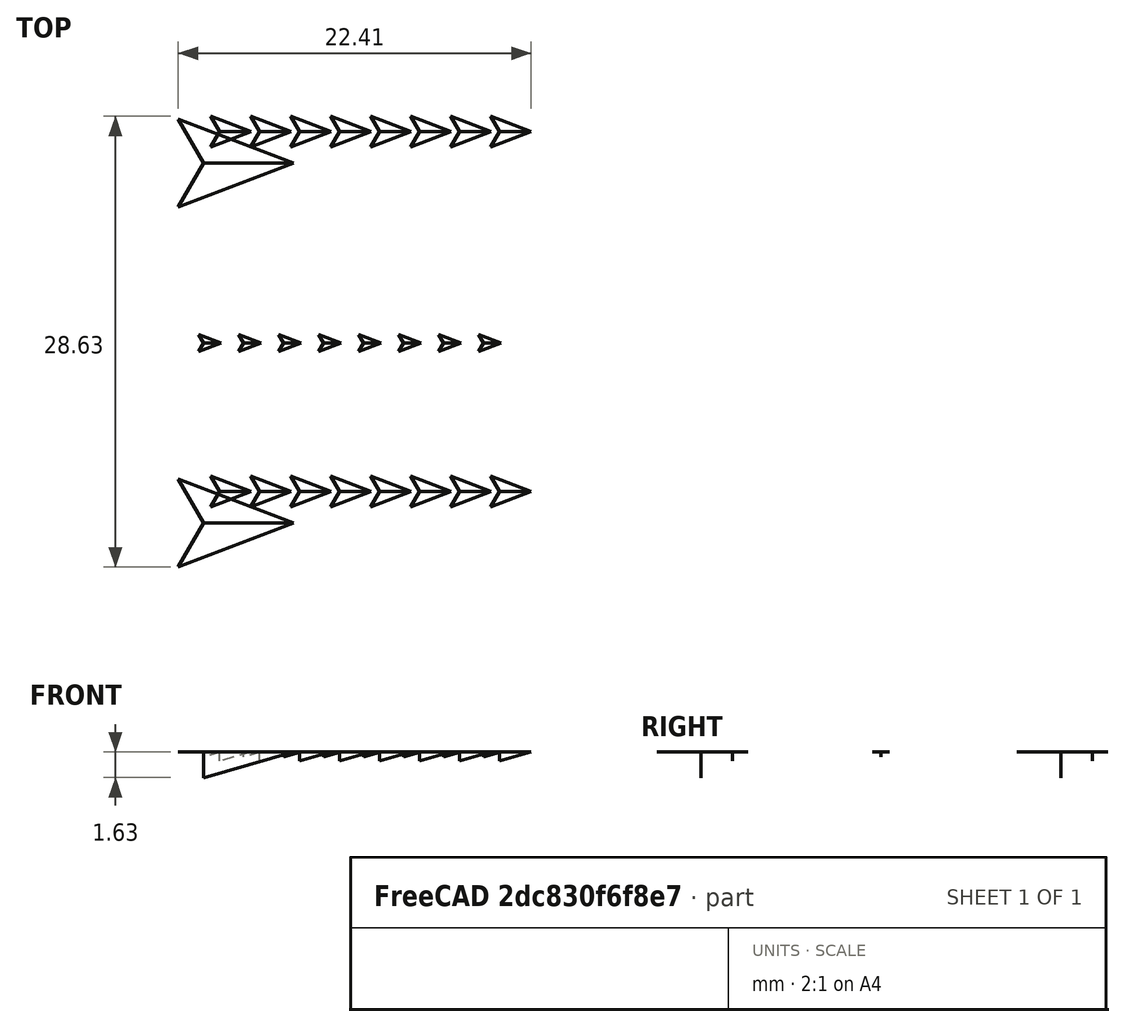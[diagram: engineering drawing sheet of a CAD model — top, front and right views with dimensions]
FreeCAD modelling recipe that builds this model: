
FCSTD DOCUMENT  (FreeCAD 0.22R34729 (Git))
Label: el_scheme_cut
License: All rights reserved
LicenseURL: http://en.wikipedia.org/wiki/All_rights_reserved
objects: Sketcher::SketchObject×3, Part::FeaturePython×3, Image::ImagePlane×1
note: 6 computed .brp shape members not serialized (recipe doc carries the construction recipe); baked Part::Feature solids carry a one-line shape summary decoded from their .brp

FEATURE [Sketcher::SketchObject] Sketch
  FullyConstrained = false
  sketch-geometry (1):
    g0: LineSegment StartX=6.30828 StartY=-11.43 StartZ=0 EndX=6.30828 EndY=11.43 EndZ=0
  constraints (2):
    c: Symmetric(g0,g0,g-1)
    c: DistanceY(g0,g0) = 22.86
FEATURE [Sketcher::SketchObject] Sketch001
  FullyConstrained = true
  sketch-geometry (5):
    g0: LineSegment StartX=34.2 StartY=-12.8 StartZ=0 EndX=34.2 EndY=12.8 EndZ=0
    g1: LineSegment StartX=34.2 StartY=12.8 StartZ=0 EndX=0 EndY=12.8 EndZ=0
    g2: LineSegment StartX=0 StartY=12.8 StartZ=0 EndX=0 EndY=-12.8 EndZ=0
    g3: LineSegment StartX=0 StartY=-12.8 StartZ=0 EndX=34.2 EndY=-12.8 EndZ=0
    g4: GeomPoint X=17.1 Y=0 Z=0
  constraints (13):
    c: Coincident(g0,g1)
    c: Coincident(g1,g2)
    c: Coincident(g2,g3)
    c: Coincident(g3,g0)
    c: Horizontal(g1)
    c: Horizontal(g3)
    c: Vertical(g0)
    c: Vertical(g2)
    c: Symmetric(g1,g0,g4)
    c: PointOnObject(g4,g-1)
    c: PointOnObject(g1,g-2)
    c: DistanceY(g2,g2) = 25.6
    c: DistanceX(g1,g1) = 34.2
FEATURE [Part::FeaturePython] LinearArray  # WARN: FeaturePython — macro-defined, semantics opaque (R4)
  Alignment = 0
  CellStart = A1
  Count = 8
  Dir = (1,0,0)
  DirIsDriven = true
  DistributionLaw = 0
  DrivenProperty = 1
  EndInclusive = true
  ExposePlacement = false
  GeneratorMode = 1
  MarkerShape = 1
  MarkerSize = 0
  NumElements = 8
  OrientMode = 1
  Point = (0,0,0)
  PointIsDriven = true
  Reverse = false
  SpanEnd = 50
  SpanStart = 0
  Step = 2.54
  Type = lattice2LinearArray.LinearArray
  VSGVersion = 1
  Values = 0.0 | 2.54 | 5.08 | 7.62 | 10.16 | 12.7 | 15.24 | 17.78
  ValuesSource = 2
  isLattice = 1
FEATURE [Part::FeaturePython] LinearArray001  # WARN: FeaturePython — macro-defined, semantics opaque (R4)
  Alignment = 0
  CellStart = A1
  Count = 2
  Dir = (0,1,0)
  DirIsDriven = true
  DistributionLaw = 0
  DrivenProperty = 1
  EndInclusive = true
  ExposePlacement = false
  GeneratorMode = 0
  MarkerShape = 1
  MarkerSize = 0
  NumElements = 2
  OrientMode = 0
  Placement = pos=(0,-11.43,0) rot=(0,0,1;0rad)
  Point = (0,0,0)
  PointIsDriven = true
  Reverse = false
  SpanEnd = 22.86
  SpanStart = 0
  Step = 22.86
  Type = lattice2LinearArray.LinearArray
  VSGVersion = 1
  Values = 0.0 | 22.86
  ValuesSource = 2
  isLattice = 1
  expr: .Placement.Base.y = -SpanEnd / 2
FEATURE [Part::FeaturePython] Populate  label="Populate LinearArray001 with LinearArray"  # WARN: FeaturePython — macro-defined, semantics opaque (R4)
  Copying = 0
  ExposePlacement = false
  MarkerShape = 1
  MarkerSize = 0
  NumElements = 16
  Object = -> LinearArray
  OutputCompounding = 0
  Placement = pos=(1,2,0) rot=(0,0,1;0rad)
  PlacementsTo = -> LinearArray001
  Referencing = 0
  Type = lattice2PopulateCopies.LatticePopulateCopies
  isLattice = 1
FEATURE [Image::ImagePlane] __02_05_43d4d8b2d99eaeb772cfaf12d7a736f88ffd931aabcc886004415b19f1957f1d_207011d827f2ce  label="0-02-05-43d4d8b2d99eaeb772cfaf12d7a736f88ffd931aabcc886004415b19f1957f1d_207011d827f2ce"
  XSize = 93.0849
  YSize = 201.537
  expr: XSize = 195.5026 mm * Sketch002.Constraints.res / Sketch002.Constraints.orig
  expr: YSize = 423.2804 mm * Sketch002.Constraints.res / Sketch002.Constraints.orig
FEATURE [Sketcher::SketchObject] Sketch002
  FullyConstrained = false
  sketch-geometry (3):
    g0: Circle CenterX=-61.0516 CenterY=40.4144 CenterZ=0 NormalX=0 NormalY=0 NormalZ=1 AngleXU=0 Radius=1.51659
    g1: Circle CenterX=-64.2277 CenterY=77.6217 CenterZ=0 NormalX=0 NormalY=0 NormalZ=1 AngleXU=0 Radius=1.58997
    g2: LineSegment StartX=-32.3209 StartY=40.3651 StartZ=0 EndX=-32.3209 EndY=58.1451 EndZ=0
  constraints (5):
    c: Block(g0)
    c: Block(g1)
    c: Distance(g1,g0) = 37.3426  'orig'
    c: DistanceY(g2,g2) = 17.78  'res'
    c: Vertical(g2)
